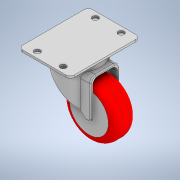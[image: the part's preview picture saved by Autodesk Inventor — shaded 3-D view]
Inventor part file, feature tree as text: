
AUTODESK INVENTOR PART (.ipt)
format: ipt  version: 2020 (Build 240168000, 168)  size: 383,488 bytes
history: native  units: mm
features: extrude x6, sketch x5, fillet x4, projected_geometry x2, other x1, hole x1
ambient origin geometry x8: Origin, YZ Plane, XZ Plane, XY Plane, X Axis, Y Axis, Z Axis, Center Point
bodies: Body1 (feature_tree)
feature tree (19):
  other  "솔리드1"
  sketch  "스케치1"
  extrude  "돌출1"  Depth=48.0mm
  hole  "구멍1"  [1 undecoded]
  extrude  "돌출2"  Depth=4.0mm
  extrude  "돌출5"  Depth=24.0mm
  extrude  "돌출6"  Depth=54.0mm
  fillet  "모깎기3"  Radius=2.0mm
  extrude  "돌출7"  Depth=40.0mm
  fillet  "모깎기4"  Radius=36.0mm
  fillet  "모깎기5"  Radius=8.0mm
  extrude  "돌출8"  Depth=27.0mm
  fillet  "모깎기7"  Radius=36.0mm
  sketch  "스케치4"
  projected_geometry  "투영된 루프1"
  sketch  "스케치5"
  projected_geometry  "투영된 루프2"
  sketch  "스케치6"
  sketch  "스케치8"
note: 1 required parameter value undecoded (feature->parameter linkage not recoverable at this tier; creation-order binding heuristic only, values carry confidence <= 0.55)
